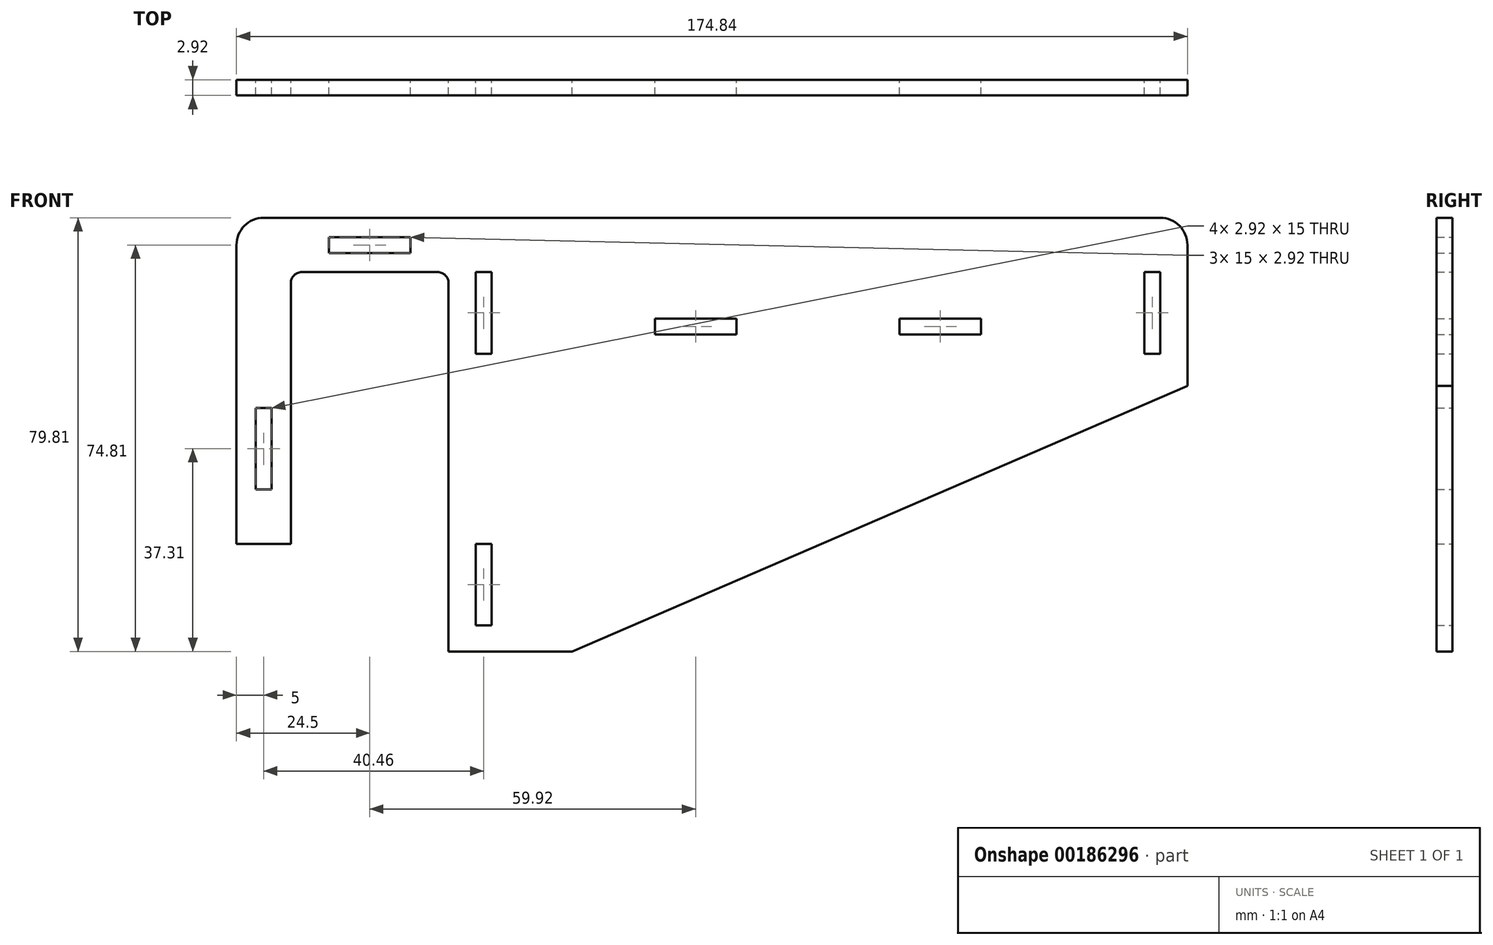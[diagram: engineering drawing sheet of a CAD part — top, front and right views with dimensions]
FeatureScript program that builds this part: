
annotation { "Feature Type Name" : "Feature", "Feature Type Description" : "" }
export const myFeature = defineFeature(function(context is Context, id is Id, definition is map)
    precondition{}
    {
        {
            assignVariable(context, id + "F0", {"name" : "e", "anyValue" : 2.92 * mm});
        }
        {
            var Q0;
            Q0=qCreatedBy(makeId("Front.planeOp"),FACE);
            var sketch = newSketch(context, id + "F1", { "sketchPlane" : qUnion([Q0])});
            skLineSegment(sketch, "E0", {"start": v(0, 0) * mm, "end": v(0, 55) * mm});
            skLineSegment(sketch, "E1", {"start": v(5, 60) * mm, "end": v(169.84, 60) * mm});
            skLineSegment(sketch, "E2", {"start": v(174.84, 55) * mm, "end": v(174.84, 29.1) * mm});
            skLineSegment(sketch, "E3", {"start": v(39, -19.81) * mm, "end": v(39, 48) * mm});
            skLineSegment(sketch, "E4", {"start": v(37, 50) * mm, "end": v(12, 50) * mm});
            skLineSegment(sketch, "E5", {"start": v(10, 48) * mm, "end": v(10, 0) * mm});
            skLineSegment(sketch, "E6", {"start": v(10, 0) * mm, "end": v(0, 0) * mm});
            skLineSegment(sketch, "E7.bottom", {"start": v(44, 50) * mm, "end": v(46.92, 50) * mm});
            skLineSegment(sketch, "E7.top", {"start": v(44, 35) * mm, "end": v(46.92, 35) * mm});
            skLineSegment(sketch, "E7.left", {"start": v(44, 50) * mm, "end": v(44, 35) * mm});
            skLineSegment(sketch, "E7.right", {"start": v(46.92, 50) * mm, "end": v(46.92, 35) * mm});
            skLineSegment(sketch, "E8.0.1.0", {"start": v(44, 0) * mm, "end": v(44, -15) * mm});
            skLineSegment(sketch, "E8.0.1.1", {"start": v(46.92, 0) * mm, "end": v(46.92, -15) * mm});
            skLineSegment(sketch, "E8.0.1.2", {"start": v(44, 0) * mm, "end": v(46.92, 0) * mm});
            skLineSegment(sketch, "E8.0.1.3", {"start": v(44, -15) * mm, "end": v(46.92, -15) * mm});
            skLineSegment(sketch, "E8.1.0.0", {"start": v(166.92, 50) * mm, "end": v(166.92, 35) * mm});
            skLineSegment(sketch, "E8.1.0.1", {"start": v(169.84, 50) * mm, "end": v(169.84, 35) * mm});
            skLineSegment(sketch, "E8.1.0.2", {"start": v(166.92, 50) * mm, "end": v(169.84, 50) * mm});
            skLineSegment(sketch, "E8.1.0.3", {"start": v(166.92, 35) * mm, "end": v(169.84, 35) * mm});
            skLineSegment(sketch, "E8.direction1", {"start": v(44, 35) * mm, "end": v(166.92, 35) * mm, "construction": true});
            skLineSegment(sketch, "E8.direction2", {"start": v(44, 35) * mm, "end": v(44, -15) * mm, "construction": true});
            skLineSegment(sketch, "E9", {"start": v(44, 35) * mm, "end": v(39, 35) * mm, "construction": true});
            skLineSegment(sketch, "E10", {"start": v(169.84, 35) * mm, "end": v(174.84, 35) * mm, "construction": true});
            skLineSegment(sketch, "E11.bottom", {"start": v(17, 56.46) * mm, "end": v(32, 56.46) * mm});
            skLineSegment(sketch, "E11.top", {"start": v(17, 53.54) * mm, "end": v(32, 53.54) * mm});
            skLineSegment(sketch, "E11.left", {"start": v(17, 56.46) * mm, "end": v(17, 53.54) * mm});
            skLineSegment(sketch, "E11.right", {"start": v(32, 56.46) * mm, "end": v(32, 53.54) * mm});
            skLineSegment(sketch, "E12.bottom", {"start": v(3.54, 25) * mm, "end": v(6.46, 25) * mm});
            skLineSegment(sketch, "E12.top", {"start": v(3.54, 10) * mm, "end": v(6.46, 10) * mm});
            skLineSegment(sketch, "E12.left", {"start": v(3.54, 25) * mm, "end": v(3.54, 10) * mm});
            skLineSegment(sketch, "E12.right", {"start": v(6.46, 25) * mm, "end": v(6.46, 10) * mm});
            skLineSegment(sketch, "E13", {"start": v(5, 10) * mm, "end": v(5, 0) * mm, "construction": true});
            skLineSegment(sketch, "E14", {"start": v(10, 50) * mm, "end": v(10, 60) * mm, "construction": true});
            skLineSegment(sketch, "E15", {"start": v(10, 55) * mm, "end": v(17, 55) * mm, "construction": true});
            skLineSegment(sketch, "E16", {"start": v(24.5, 53.54) * mm, "end": v(24.5, 50) * mm, "construction": true});
            skPoint(sketch, "E17.visualSharp", {"position": v(0, 60) * mm});
            skArc(sketch, "E17.filletArc", {"start": v(5, 60) * mm, "mid": v(1.46, 58.54) * mm, "end": v(0, 55) * mm});
            skPoint(sketch, "E18.visualSharp", {"position": v(10, 50) * mm});
            skArc(sketch, "E18.filletArc", {"start": v(12, 50) * mm, "mid": v(10.59, 49.41) * mm, "end": v(10, 48) * mm});
            skPoint(sketch, "E19.visualSharp", {"position": v(39, 50) * mm});
            skArc(sketch, "E19.filletArc", {"start": v(39, 48) * mm, "mid": v(38.41, 49.41) * mm, "end": v(37, 50) * mm});
            skPoint(sketch, "E20.visualSharp", {"position": v(174.84, 60) * mm});
            skArc(sketch, "E20.filletArc", {"start": v(174.84, 55) * mm, "mid": v(173.38, 58.54) * mm, "end": v(169.84, 60) * mm});
            skLineSegment(sketch, "E21", {"start": v(39, -19.81) * mm, "end": v(61.74, -19.81) * mm});
            skLineSegment(sketch, "E22", {"start": v(61.74, -19.81) * mm, "end": v(174.84, 29.1) * mm});
            skLineSegment(sketch, "E23.bottom", {"start": v(76.92, 41.46) * mm, "end": v(91.92, 41.46) * mm});
            skLineSegment(sketch, "E23.top", {"start": v(76.92, 38.54) * mm, "end": v(91.92, 38.54) * mm});
            skLineSegment(sketch, "E23.left", {"start": v(76.92, 41.46) * mm, "end": v(76.92, 38.54) * mm});
            skLineSegment(sketch, "E23.right", {"start": v(91.92, 41.46) * mm, "end": v(91.92, 38.54) * mm});
            skLineSegment(sketch, "E24.bottom", {"start": v(121.92, 41.46) * mm, "end": v(136.92, 41.46) * mm});
            skLineSegment(sketch, "E24.top", {"start": v(121.92, 38.54) * mm, "end": v(136.92, 38.54) * mm});
            skLineSegment(sketch, "E24.left", {"start": v(121.92, 41.46) * mm, "end": v(121.92, 38.54) * mm});
            skLineSegment(sketch, "E24.right", {"start": v(136.92, 41.46) * mm, "end": v(136.92, 38.54) * mm});
            skPoint(sketch, "E25", {"position": v(76.92, 40) * mm});
            skLineSegment(sketch, "E26", {"start": v(106.92, 65.33) * mm, "end": v(106.92, -13.93) * mm, "construction": true});
            skSolve(sketch);
        }
        {
            var Q0;
            Q0=qSketchRegion(id+"F1",true);
            extrude(context, id + "F2", {"entities" : qUnion([Q0]), "depth" : (getVariable(context, 'e'))});
        }
    });
